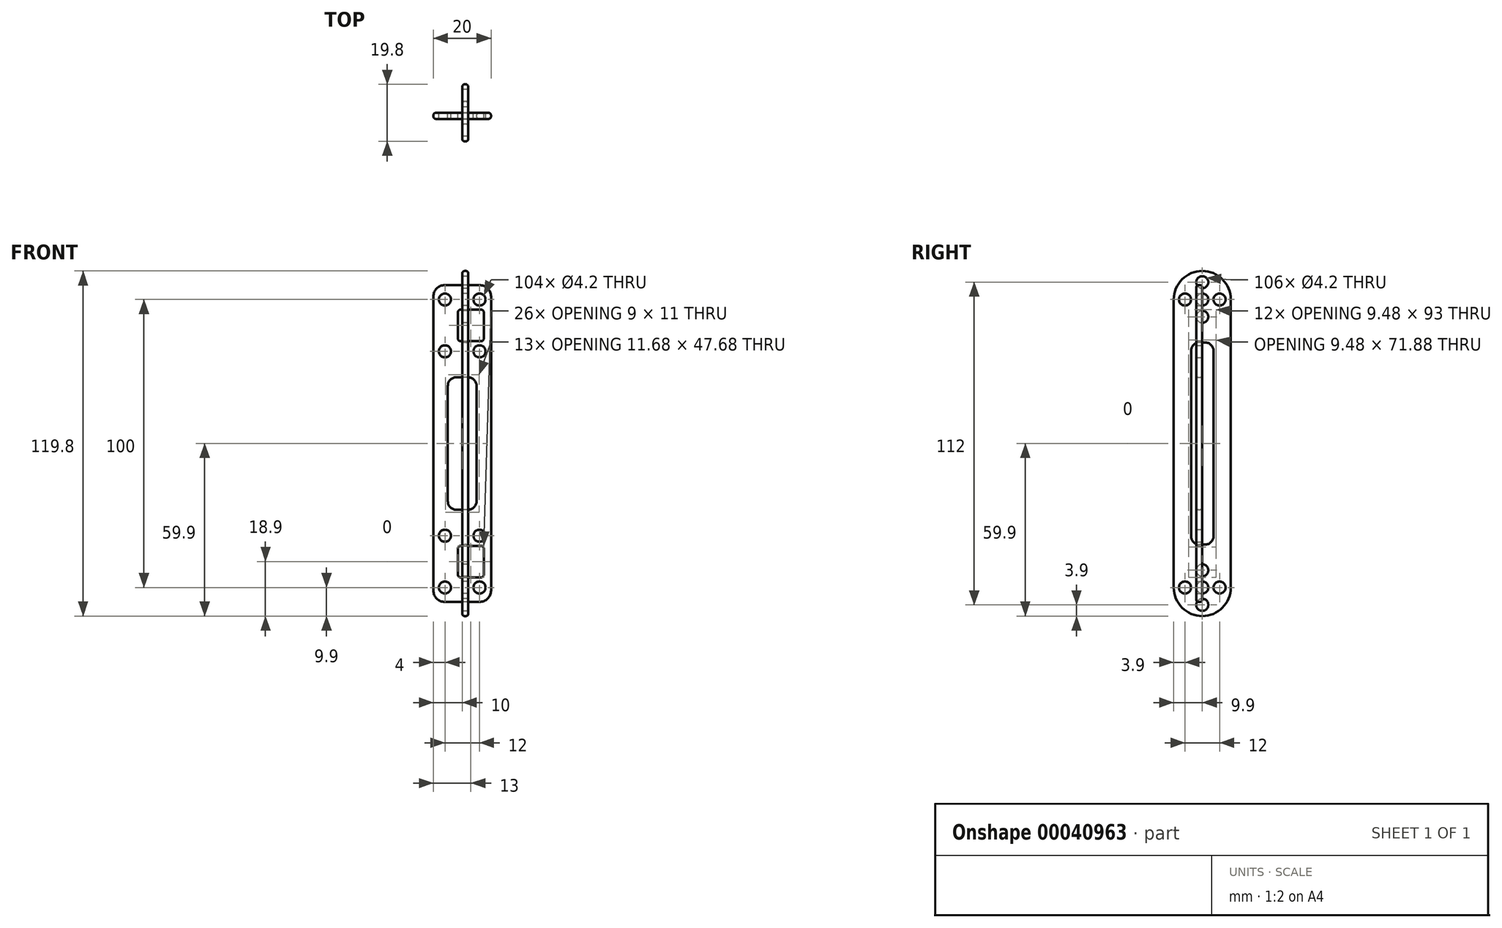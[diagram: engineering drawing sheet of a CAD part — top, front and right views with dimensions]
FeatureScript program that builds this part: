
annotation { "Feature Type Name" : "Feature", "Feature Type Description" : "" }
export const myFeature = defineFeature(function(context is Context, id is Id, definition is map)
    precondition{}
    {
        {
            assignVariable(context, id + "F0", {"name" : "tolerance", "anyValue" : 0.1});
        }
        {
            assignVariable(context, id + "F1", {"name" : "thickness", "anyValue" : 2.2 - getVariable(context, 'tolerance')});
        }
        {
            var Q0;
            Q0=qCreatedBy(makeId("Right.planeOp"),FACE);
            var sketch = newSketch(context, id + "F2", { "sketchPlane" : qUnion([Q0])});
            skLineSegment(sketch, "E0.rect.bottom", {"start": v(12, -9) * mm, "end": v(-12, -9) * mm});
            skLineSegment(sketch, "E0.rect.top", {"start": v(12, 27) * mm, "end": v(-12, 27) * mm});
            skLineSegment(sketch, "E0.rect.left", {"start": v(12, -9) * mm, "end": v(12, 27) * mm});
            skLineSegment(sketch, "E0.rect.right", {"start": v(-12, -9) * mm, "end": v(-12, 27) * mm});
            skPoint(sketch, "E0.rect.middle", {"position": v(0, 9) * mm});
            skCircle(sketch, "E1", {"center": v(0, 0) * mm, "radius": 8.9 * mm});
            skLineSegment(sketch, "E2", {"start": v(0, 27) * mm, "end": v(0, -9) * mm, "construction": true});
            skCircle(sketch, "E3", {"center": v(0, 0) * mm, "radius": 6 * mm, "construction": true});
            skCircle(sketch, "E4", {"center": v(0, -6) * mm, "radius": 2 * mm});
            skCircle(sketch, "E5.1.0", {"center": v(6, 0) * mm, "radius": 2 * mm});
            skCircle(sketch, "E5.2.0", {"center": v(0, 6) * mm, "radius": 2 * mm});
            skCircle(sketch, "E5.3.0", {"center": v(-6, 0) * mm, "radius": 2 * mm});
            skCircle(sketch, "E6", {"center": v(-4.24, 4.24) * mm, "radius": 0.8 * mm});
            skCircle(sketch, "E7.1.0", {"center": v(-4.24, -4.24) * mm, "radius": 0.8 * mm});
            skCircle(sketch, "E7.2.0", {"center": v(4.24, -4.24) * mm, "radius": 0.8 * mm});
            skCircle(sketch, "E7.3.0", {"center": v(4.24, 4.24) * mm, "radius": 0.8 * mm});
            skLineSegment(sketch, "E8", {"start": v(-6, 24) * mm, "end": v(6, 24) * mm, "construction": true});
            skCircle(sketch, "E9", {"center": v(-6, 24) * mm, "radius": 2 * mm});
            skCircle(sketch, "E10", {"center": v(0, 24) * mm, "radius": 2 * mm});
            skCircle(sketch, "E11", {"center": v(6, 24) * mm, "radius": 2 * mm});
            skPoint(sketch, "E12.center", {"position": v(0, 100) * mm});
            skLineSegment(sketch, "E13.rect.right", {"start": v(12, 109) * mm, "end": v(12, 73) * mm});
            skCircle(sketch, "E14", {"center": v(-6, 76) * mm, "radius": 2 * mm});
            skLineSegment(sketch, "E15", {"start": v(0, 73) * mm, "end": v(0, 109) * mm, "construction": true});
            skCircle(sketch, "E16", {"center": v(0, 100) * mm, "radius": 8.9 * mm});
            skLineSegment(sketch, "E13.rect.left", {"start": v(-12, 109) * mm, "end": v(-12, 73) * mm});
            skLineSegment(sketch, "E13.rect.bottom", {"start": v(-12, 109) * mm, "end": v(12, 109) * mm});
            skLineSegment(sketch, "E13.rect.top", {"start": v(-12, 73) * mm, "end": v(12, 73) * mm});
            skLineSegment(sketch, "E17", {"start": v(6, 76) * mm, "end": v(-6, 76) * mm, "construction": true});
            skCircle(sketch, "E18", {"center": v(0, 76) * mm, "radius": 2 * mm});
            skPoint(sketch, "E13.rect.middle", {"position": v(0, 91) * mm});
            skCircle(sketch, "E12.2.0", {"center": v(0, 94) * mm, "radius": 2 * mm});
            skCircle(sketch, "E12.1.0", {"center": v(-6, 100) * mm, "radius": 2 * mm});
            skCircle(sketch, "E19", {"center": v(0, 100) * mm, "radius": 6 * mm, "construction": true});
            skCircle(sketch, "E20", {"center": v(0, 106) * mm, "radius": 2 * mm});
            skCircle(sketch, "E21", {"center": v(-4.24, 104.24) * mm, "radius": 0.8 * mm});
            skCircle(sketch, "E12.3.0", {"center": v(6, 100) * mm, "radius": 2 * mm});
            skCircle(sketch, "E22.3.0", {"center": v(4.24, 104.24) * mm, "radius": 0.8 * mm});
            skCircle(sketch, "E22.2.0", {"center": v(4.24, 95.76) * mm, "radius": 0.8 * mm});
            skCircle(sketch, "E22.1.0", {"center": v(-4.24, 95.76) * mm, "radius": 0.8 * mm});
            skCircle(sketch, "E23", {"center": v(6, 76) * mm, "radius": 2 * mm});
            skSolve(sketch);
        }
        {
            var Q0;
            Q0=qCreatedBy(makeId("Front.planeOp"),FACE);
            var sketch = newSketch(context, id + "F3", { "sketchPlane" : qUnion([Q0])});
            skLineSegment(sketch, "E24", {"start": v(0, 22.5) * mm, "end": v(9, 22.5) * mm});
            skLineSegment(sketch, "E25", {"start": v(9, 22.5) * mm, "end": v(9, 27) * mm});
            skLineSegment(sketch, "E26", {"start": v(9, 27) * mm, "end": v(12, 27) * mm});
            skLineSegment(sketch, "E27", {"start": v(12, 27) * mm, "end": v(12, -9) * mm});
            skLineSegment(sketch, "E28", {"start": v(12, -9) * mm, "end": v(0, -9) * mm});
            skLineSegment(sketch, "E29", {"start": v(12, 8.9) * mm, "end": v(15, 8.9) * mm});
            skLineSegment(sketch, "E30", {"start": v(15, 8.9) * mm, "end": v(15, -8.9) * mm});
            skLineSegment(sketch, "E31", {"start": v(15, -8.9) * mm, "end": v(12, -8.9) * mm});
            skLineSegment(sketch, "E32", {"start": v(0, 1.45) * mm, "end": v(0, -56.88) * mm, "construction": true});
            skLineSegment(sketch, "E33", {"start": v(0, 0) * mm, "end": v(15, 0) * mm, "construction": true});
            skLineSegment(sketch, "E34.MirrorCS", {"start": v(-15, 8.9) * mm, "end": v(-15, -8.9) * mm});
            skLineSegment(sketch, "E35.MirrorCS", {"start": v(0, 22.5) * mm, "end": v(-9, 22.5) * mm});
            skLineSegment(sketch, "E36.MirrorCS", {"start": v(0, 0) * mm, "end": v(-15, 0) * mm, "construction": true});
            skLineSegment(sketch, "E37.MirrorCS", {"start": v(-9, 22.5) * mm, "end": v(-9, 27) * mm});
            skLineSegment(sketch, "E38.MirrorCS", {"start": v(-12, 8.9) * mm, "end": v(-15, 8.9) * mm});
            skLineSegment(sketch, "E39.MirrorCS", {"start": v(-12, -9) * mm, "end": v(0, -9) * mm});
            skLineSegment(sketch, "E40.MirrorCS", {"start": v(-12, 27) * mm, "end": v(-12, -9) * mm});
            skLineSegment(sketch, "E41.MirrorCS", {"start": v(-15, -8.9) * mm, "end": v(-12, -8.9) * mm});
            skLineSegment(sketch, "E42.MirrorCS", {"start": v(-9, 27) * mm, "end": v(-12, 27) * mm});
            skLineSegment(sketch, "E43.MirrorCS", {"start": v(0, 100) * mm, "end": v(-15, 100) * mm, "construction": true});
            skLineSegment(sketch, "E44.MirrorCS", {"start": v(0, 77.5) * mm, "end": v(-9, 77.5) * mm});
            skLineSegment(sketch, "E45", {"start": v(15, 108.9) * mm, "end": v(15, 91.1) * mm});
            skLineSegment(sketch, "E46.MirrorCS", {"start": v(-15, 108.9) * mm, "end": v(-15, 91.1) * mm});
            skLineSegment(sketch, "E47", {"start": v(0, 57.8) * mm, "end": v(0, 0) * mm, "construction": true});
            skLineSegment(sketch, "E48", {"start": v(12, 109) * mm, "end": v(0, 109) * mm});
            skLineSegment(sketch, "E49", {"start": v(12, 109) * mm, "end": v(12, 73) * mm});
            skLineSegment(sketch, "E50", {"start": v(0, 77.5) * mm, "end": v(9, 77.5) * mm});
            skLineSegment(sketch, "E51.MirrorCS", {"start": v(-12, 109) * mm, "end": v(0, 109) * mm});
            skLineSegment(sketch, "E52.MirrorCS", {"start": v(-12, 109) * mm, "end": v(-12, 73) * mm});
            skLineSegment(sketch, "E53", {"start": v(0, 100) * mm, "end": v(15, 100) * mm, "construction": true});
            skLineSegment(sketch, "E54", {"start": v(12, 108.9) * mm, "end": v(15, 108.9) * mm});
            skLineSegment(sketch, "E55", {"start": v(9, 73) * mm, "end": v(12, 73) * mm});
            skLineSegment(sketch, "E56", {"start": v(9, 73) * mm, "end": v(9, 77.5) * mm});
            skLineSegment(sketch, "E57.MirrorCS", {"start": v(-9, 73) * mm, "end": v(-12, 73) * mm});
            skLineSegment(sketch, "E58.MirrorCS", {"start": v(-12, 108.9) * mm, "end": v(-15, 108.9) * mm});
            skLineSegment(sketch, "E59.MirrorCS", {"start": v(-9, 73) * mm, "end": v(-9, 77.5) * mm});
            skLineSegment(sketch, "E60.MirrorCS", {"start": v(-15, 91.1) * mm, "end": v(-12, 91.1) * mm});
            skLineSegment(sketch, "E61", {"start": v(15, 91.1) * mm, "end": v(12, 91.1) * mm});
            skLineSegment(sketch, "E62.bottom", {"start": v(-6, 18) * mm, "end": v(6, 18) * mm, "construction": true});
            skLineSegment(sketch, "E62.top", {"start": v(-6, 0) * mm, "end": v(6, 0) * mm, "construction": true});
            skLineSegment(sketch, "E62.left", {"start": v(-6, 18) * mm, "end": v(-6, 0) * mm, "construction": true});
            skLineSegment(sketch, "E62.right", {"start": v(6, 18) * mm, "end": v(6, 0) * mm, "construction": true});
            skCircle(sketch, "E63", {"center": v(6, 0) * mm, "radius": 2 * mm});
            skCircle(sketch, "E64", {"center": v(-6, 0) * mm, "radius": 2 * mm});
            skCircle(sketch, "E65", {"center": v(-6, 18) * mm, "radius": 2 * mm});
            skCircle(sketch, "E66", {"center": v(6, 18) * mm, "radius": 2 * mm});
            skLineSegment(sketch, "E67.left", {"start": v(-6, 100) * mm, "end": v(-6, 82) * mm, "construction": true});
            skCircle(sketch, "E68", {"center": v(-6, 100) * mm, "radius": 2 * mm});
            skLineSegment(sketch, "E67.right", {"start": v(6, 100) * mm, "end": v(6, 82) * mm, "construction": true});
            skLineSegment(sketch, "E67.bottom", {"start": v(-6, 100) * mm, "end": v(6, 100) * mm, "construction": true});
            skCircle(sketch, "E69", {"center": v(6, 100) * mm, "radius": 2 * mm});
            skCircle(sketch, "E70", {"center": v(6, 82) * mm, "radius": 2 * mm});
            skLineSegment(sketch, "E67.top", {"start": v(-6, 82) * mm, "end": v(6, 82) * mm, "construction": true});
            skCircle(sketch, "E71", {"center": v(-6, 82) * mm, "radius": 2 * mm});
            skLineSegment(sketch, "E72.rect.bottom", {"start": v(7.5, 96.5) * mm, "end": v(-7.5, 96.5) * mm});
            skLineSegment(sketch, "E72.rect.top", {"start": v(7.5, 85.5) * mm, "end": v(-7.5, 85.5) * mm});
            skLineSegment(sketch, "E72.rect.left", {"start": v(7.5, 96.5) * mm, "end": v(7.5, 85.5) * mm});
            skLineSegment(sketch, "E72.rect.right", {"start": v(-7.5, 96.5) * mm, "end": v(-7.5, 85.5) * mm});
            skPoint(sketch, "E72.rect.middle", {"position": v(0, 91) * mm});
            skLineSegment(sketch, "E73.rect.bottom", {"start": v(7.5, 3.5) * mm, "end": v(-7.5, 3.5) * mm});
            skLineSegment(sketch, "E73.rect.top", {"start": v(7.5, 14.5) * mm, "end": v(-7.5, 14.5) * mm});
            skLineSegment(sketch, "E73.rect.left", {"start": v(7.5, 3.5) * mm, "end": v(7.5, 14.5) * mm});
            skLineSegment(sketch, "E73.rect.right", {"start": v(-7.5, 3.5) * mm, "end": v(-7.5, 14.5) * mm});
            skPoint(sketch, "E73.rect.middle", {"position": v(0, 9) * mm});
            skSolve(sketch);
        }
        {
            var Q0;
            Q0=qCreatedBy(makeId("Front.planeOp"),FACE);
            var sketch = newSketch(context, id + "F4", { "sketchPlane" : qUnion([Q0])});
            skLineSegment(sketch, "E74.rect.bottom", {"start": v(6, 105) * mm, "end": v(-6, 105) * mm});
            skLineSegment(sketch, "E74.rect.top", {"start": v(6, -5) * mm, "end": v(-6, -5) * mm});
            skLineSegment(sketch, "E74.rect.left", {"start": v(10, 101) * mm, "end": v(10, -1) * mm});
            skLineSegment(sketch, "E74.rect.right", {"start": v(-10, 101) * mm, "end": v(-10, -1) * mm});
            skPoint(sketch, "E74.rect.middle", {"position": v(0, 50) * mm});
            skCircle(sketch, "E75", {"center": v(-6, 18) * mm, "radius": 2.1 * mm});
            skCircle(sketch, "E76", {"center": v(6, 18) * mm, "radius": 2.1 * mm});
            skCircle(sketch, "E77", {"center": v(-6, 0) * mm, "radius": 2.1 * mm});
            skCircle(sketch, "E78", {"center": v(6, 0) * mm, "radius": 2.1 * mm});
            skCircle(sketch, "E79", {"center": v(-6, 82) * mm, "radius": 2.1 * mm});
            skCircle(sketch, "E80", {"center": v(6, 82) * mm, "radius": 2.1 * mm});
            skCircle(sketch, "E81", {"center": v(-6, 100) * mm, "radius": 2.1 * mm});
            skCircle(sketch, "E82", {"center": v(6, 100) * mm, "radius": 2.1 * mm});
            skPoint(sketch, "E83.visualSharp", {"position": v(-10, 105) * mm});
            skArc(sketch, "E83.filletArc", {"start": v(-6, 105) * mm, "mid": v(-8.83, 103.83) * mm, "end": v(-10, 101) * mm});
            skPoint(sketch, "E84.visualSharp", {"position": v(10, 105) * mm});
            skArc(sketch, "E84.filletArc", {"start": v(10, 101) * mm, "mid": v(8.83, 103.83) * mm, "end": v(6, 105) * mm});
            skPoint(sketch, "E85.visualSharp", {"position": v(10, -5) * mm});
            skArc(sketch, "E85.filletArc", {"start": v(6, -5) * mm, "mid": v(8.83, -3.83) * mm, "end": v(10, -1) * mm});
            skPoint(sketch, "E86.visualSharp", {"position": v(-10, -5) * mm});
            skArc(sketch, "E86.filletArc", {"start": v(-10, -1) * mm, "mid": v(-8.83, -3.83) * mm, "end": v(-6, -5) * mm});
            skLineSegment(sketch, "E87.rect.bottom", {"start": v(2, 27) * mm, "end": v(-2, 27) * mm});
            skLineSegment(sketch, "E87.rect.top", {"start": v(2, 73) * mm, "end": v(-2, 73) * mm});
            skLineSegment(sketch, "E87.rect.left", {"start": v(5, 30) * mm, "end": v(5, 70) * mm});
            skLineSegment(sketch, "E87.rect.right", {"start": v(-5, 30) * mm, "end": v(-5, 70) * mm});
            skPoint(sketch, "E88.visualSharp", {"position": v(-5, 73) * mm});
            skArc(sketch, "E88.filletArc", {"start": v(-2, 73) * mm, "mid": v(-4.12, 72.12) * mm, "end": v(-5, 70) * mm});
            skPoint(sketch, "E89.visualSharp", {"position": v(5, 73) * mm});
            skArc(sketch, "E89.filletArc", {"start": v(5, 70) * mm, "mid": v(4.12, 72.12) * mm, "end": v(2, 73) * mm});
            skPoint(sketch, "E90.visualSharp", {"position": v(5, 27) * mm});
            skArc(sketch, "E90.filletArc", {"start": v(2, 27) * mm, "mid": v(4.12, 27.88) * mm, "end": v(5, 30) * mm});
            skPoint(sketch, "E91.visualSharp", {"position": v(-5, 27) * mm});
            skArc(sketch, "E91.filletArc", {"start": v(-5, 30) * mm, "mid": v(-4.12, 27.88) * mm, "end": v(-2, 27) * mm});
            skSolve(sketch);
        }
        {
            var Q0;
            Q0=makeQuery(id+"F4.imprint","IMPRINT",FACE,{"disambiguationData":[TD([[makeQuery(id+"F4.imprint","IMPRINT",EDGE,{"derivedFrom":sQuery(id+"F4.wireOp",EDGE,"E74.rect.bottom")}),1.0]])]});
            extrude(context, id + "F5", {"entities" : qUnion([Q0]), "depth" : (getVariable(context, 'thickness')) * mm});
        }
        {
            var Q0;
            Q0=qCreatedBy(makeId("Front.planeOp"),FACE);
            var sketch = newSketch(context, id + "F6", { "sketchPlane" : qUnion([Q0])});
            skLineSegment(sketch, "E92.rect.bottom", {"start": v(-0.5, 14.5) * mm, "end": v(6.5, 14.5) * mm});
            skLineSegment(sketch, "E92.rect.top", {"start": v(-0.5, 3.5) * mm, "end": v(6.5, 3.5) * mm});
            skLineSegment(sketch, "E92.rect.left", {"start": v(-1.5, 13.5) * mm, "end": v(-1.5, 4.5) * mm});
            skLineSegment(sketch, "E92.rect.right", {"start": v(7.5, 13.5) * mm, "end": v(7.5, 4.5) * mm});
            skPoint(sketch, "E92.rect.middle", {"position": v(3, 9) * mm});
            skPoint(sketch, "E93.visualSharp", {"position": v(-1.5, 14.5) * mm});
            skArc(sketch, "E93.filletArc", {"start": v(-0.5, 14.5) * mm, "mid": v(-1.2, 14.2) * mm, "end": v(-1.5, 13.5) * mm});
            skPoint(sketch, "E94.visualSharp", {"position": v(7.5, 14.5) * mm});
            skArc(sketch, "E94.filletArc", {"start": v(7.5, 13.5) * mm, "mid": v(7.2, 14.2) * mm, "end": v(6.5, 14.5) * mm});
            skPoint(sketch, "E95.visualSharp", {"position": v(7.5, 3.5) * mm});
            skArc(sketch, "E95.filletArc", {"start": v(6.5, 3.5) * mm, "mid": v(7.2, 3.8) * mm, "end": v(7.5, 4.5) * mm});
            skPoint(sketch, "E96.visualSharp", {"position": v(-1.5, 3.5) * mm});
            skArc(sketch, "E96.filletArc", {"start": v(-1.5, 4.5) * mm, "mid": v(-1.2, 3.8) * mm, "end": v(-0.5, 3.5) * mm});
            skPoint(sketch, "E97.visualSharp", {"position": v(7.5, 96.5) * mm});
            skPoint(sketch, "E98.visualSharp", {"position": v(-1.5, 85.5) * mm});
            skPoint(sketch, "E99.rect.middle", {"position": v(3, 91) * mm});
            skPoint(sketch, "E100.visualSharp", {"position": v(7.5, 85.5) * mm});
            skLineSegment(sketch, "E99.rect.top", {"start": v(-0.5, 85.5) * mm, "end": v(6.5, 85.5) * mm});
            skLineSegment(sketch, "E99.rect.right", {"start": v(7.5, 95.5) * mm, "end": v(7.5, 86.5) * mm});
            skPoint(sketch, "E101.visualSharp", {"position": v(-1.5, 96.5) * mm});
            skLineSegment(sketch, "E99.rect.bottom", {"start": v(-0.5, 96.5) * mm, "end": v(6.5, 96.5) * mm});
            skLineSegment(sketch, "E99.rect.left", {"start": v(-1.5, 95.5) * mm, "end": v(-1.5, 86.5) * mm});
            skArc(sketch, "E98.filletArc", {"start": v(-1.5, 86.5) * mm, "mid": v(-1.2, 85.8) * mm, "end": v(-0.5, 85.5) * mm});
            skArc(sketch, "E101.filletArc", {"start": v(-0.5, 96.5) * mm, "mid": v(-1.2, 96.2) * mm, "end": v(-1.5, 95.5) * mm});
            skArc(sketch, "E97.filletArc", {"start": v(7.5, 95.5) * mm, "mid": v(7.2, 96.2) * mm, "end": v(6.5, 96.5) * mm});
            skArc(sketch, "E100.filletArc", {"start": v(6.5, 85.5) * mm, "mid": v(7.2, 85.8) * mm, "end": v(7.5, 86.5) * mm});
            skSolve(sketch);
        }
        {
            var Q0;
            Q0 = qSketchRegion(id + "F6", true);
            extrude(context, id + "F7", {"entities" : qUnion([Q0]), "operationType" : NewBodyOperationType.REMOVE, "endBound" : BoundingType.UP_TO_NEXT, "depth" : 25 * mm});
        }
        {
            var Q0;
            Q0=makeQuery(id+"F5.opExtrude","SWEPT_FACE",FACE,{"disambiguationData":[OSD([sQuery(id+"F4.wireOp",EDGE,"E74.rect.left")])]});
            var Q1;
            Q1=makeQuery(id+"F5.opExtrude","SWEPT_FACE",FACE,{"disambiguationData":[OSD([sQuery(id+"F4.wireOp",EDGE,"E87.rect.right")])]});
            fillet(context, id + "F8", {"entities" : qUnion([Q0, Q1]), "radius" : (getVariable(context, 'thickness') / 2.5) * mm, "tangentPropagation" : true, "allowEdgeOverflow" : false});
        }
        {
            var Q0;
            Q0=qCreatedBy(makeId("Right.planeOp"),FACE);
            var sketch = newSketch(context, id + "F9", { "sketchPlane" : qUnion([Q0])});
            skCircle(sketch, "E102", {"center": v(0, 100) * mm, "radius": 9.9 * mm});
            skCircle(sketch, "E103", {"center": v(0, 0) * mm, "radius": 9.9 * mm});
            skLineSegment(sketch, "E104", {"start": v(9.9, 0) * mm, "end": v(9.9, 100) * mm});
            skLineSegment(sketch, "E105", {"start": v(-9.9, 100) * mm, "end": v(-9.9, 0) * mm});
            skCircle(sketch, "E106", {"center": v(0, 106) * mm, "radius": 2.1 * mm});
            skCircle(sketch, "E107", {"center": v(-6, 100) * mm, "radius": 2.1 * mm});
            skCircle(sketch, "E108", {"center": v(6, 100) * mm, "radius": 2.1 * mm});
            skCircle(sketch, "E109", {"center": v(0, 94) * mm, "radius": 2.1 * mm});
            skCircle(sketch, "E110", {"center": v(-6, 0) * mm, "radius": 2.1 * mm});
            skCircle(sketch, "E111", {"center": v(0, 6) * mm, "radius": 2.1 * mm});
            skCircle(sketch, "E112", {"center": v(6, 0) * mm, "radius": 2.1 * mm});
            skCircle(sketch, "E113", {"center": v(0, -6) * mm, "radius": 2.1 * mm});
            skCircle(sketch, "E114", {"center": v(0, 100) * mm, "radius": 2.1 * mm});
            skCircle(sketch, "E115", {"center": v(0, 0) * mm, "radius": 2.1 * mm});
            skLineSegment(sketch, "E116.rect.bottom", {"start": v(0.9, 14.9) * mm, "end": v(-0.9, 14.9) * mm});
            skLineSegment(sketch, "E116.rect.top", {"start": v(0.9, 85.1) * mm, "end": v(-0.9, 85.1) * mm});
            skLineSegment(sketch, "E116.rect.left", {"start": v(3.9, 17.9) * mm, "end": v(3.9, 82.1) * mm});
            skLineSegment(sketch, "E116.rect.right", {"start": v(-3.9, 17.9) * mm, "end": v(-3.9, 82.1) * mm});
            skPoint(sketch, "E116.rect.middle", {"position": v(0, 50) * mm});
            skLineSegment(sketch, "E117", {"start": v(0, 100) * mm, "end": v(0, 0) * mm, "construction": true});
            skPoint(sketch, "E118.visualSharp", {"position": v(-3.9, 14.9) * mm});
            skArc(sketch, "E118.filletArc", {"start": v(-3.9, 17.9) * mm, "mid": v(-3.02, 15.78) * mm, "end": v(-0.9, 14.9) * mm});
            skPoint(sketch, "E119.visualSharp", {"position": v(3.9, 14.9) * mm});
            skArc(sketch, "E119.filletArc", {"start": v(0.9, 14.9) * mm, "mid": v(3.02, 15.78) * mm, "end": v(3.9, 17.9) * mm});
            skPoint(sketch, "E120.visualSharp", {"position": v(-3.9, 85.1) * mm});
            skArc(sketch, "E120.filletArc", {"start": v(-0.9, 85.1) * mm, "mid": v(-3.02, 84.22) * mm, "end": v(-3.9, 82.1) * mm});
            skPoint(sketch, "E121.visualSharp", {"position": v(3.9, 85.1) * mm});
            skArc(sketch, "E121.filletArc", {"start": v(3.9, 82.1) * mm, "mid": v(3.02, 84.22) * mm, "end": v(0.9, 85.1) * mm});
            skSolve(sketch);
        }
        {
            var Q0;
            Q0 = qSketchRegion(id + "F9", true);
            extrude(context, id + "F10", {"entities" : qUnion([Q0]), "depth" : (getVariable(context, 'thickness')) * mm});
        }
        {
            var Q0;
            Q0=makeQuery(id+"F10.opExtrude","SWEPT_FACE",FACE,{"disambiguationData":[OSD([sQuery(id+"F9.wireOp",EDGE,"E104")])]});
            var Q1;
            Q1=makeQuery(id+"F10.opExtrude","SWEPT_FACE",FACE,{"disambiguationData":[OSD([sQuery(id+"F9.wireOp",EDGE,"E116.rect.right")])]});
            fillet(context, id + "F11", {"entities" : qUnion([Q0, Q1]), "radius" : (getVariable(context, 'thickness') / 2.5) * mm, "tangentPropagation" : true, "allowEdgeOverflow" : false});
        }
    });
